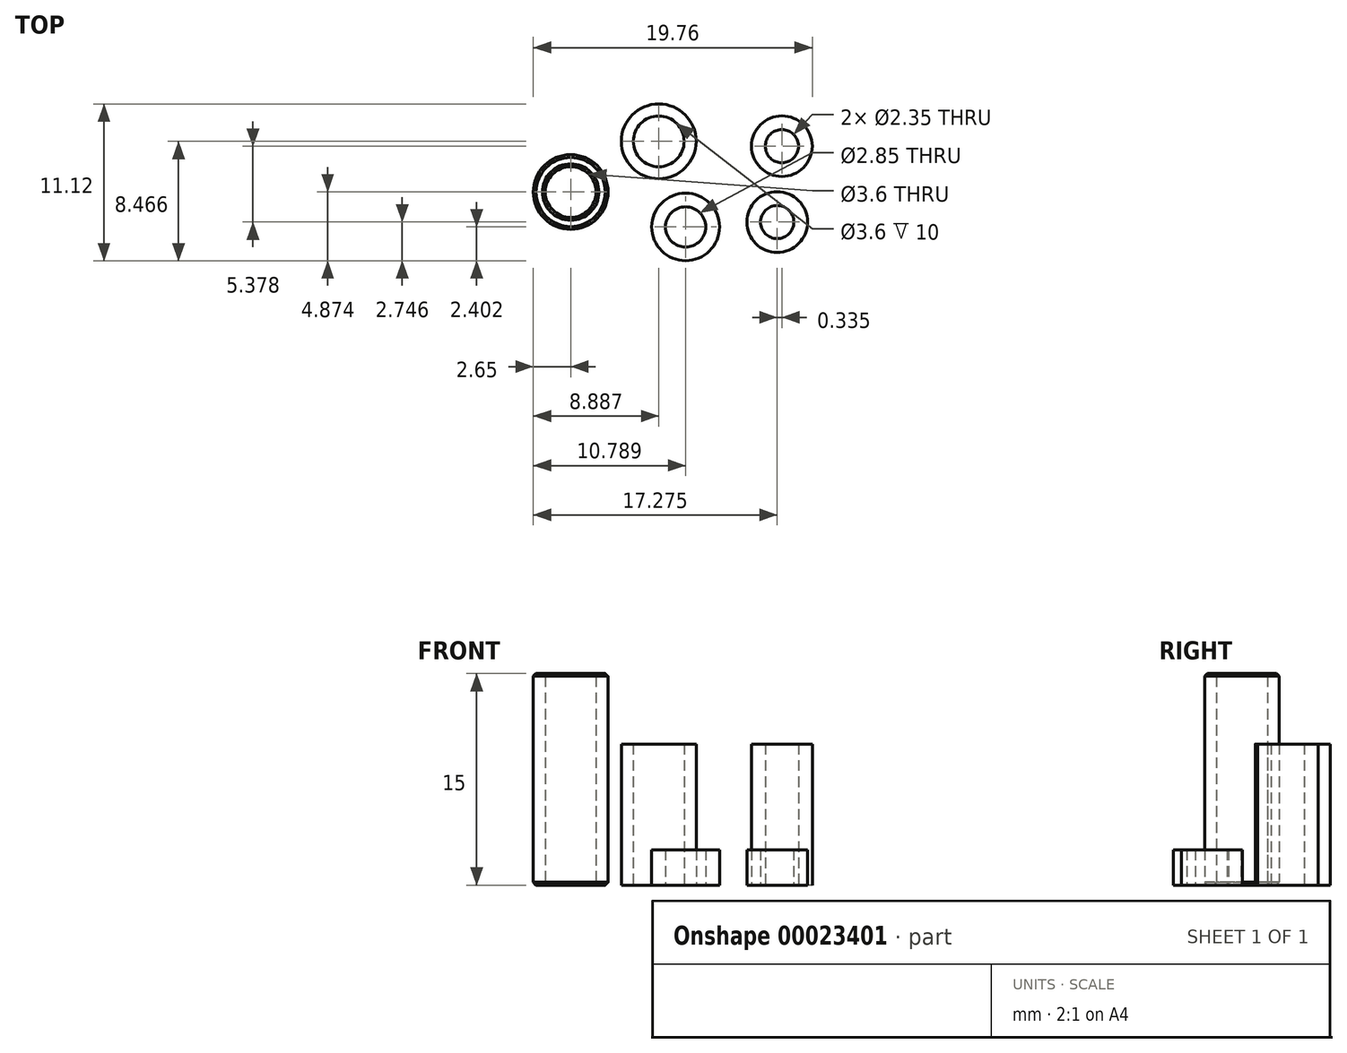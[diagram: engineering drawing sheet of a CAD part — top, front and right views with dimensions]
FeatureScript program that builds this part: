
annotation { "Feature Type Name" : "Feature", "Feature Type Description" : "" }
export const myFeature = defineFeature(function(context is Context, id is Id, definition is map)
    precondition{}
    {
        {
            var Q0;
            Q0=qCreatedBy(makeId("Top.planeOp"),FACE);
            var sketch = newSketch(context, id + "F0", { "sketchPlane" : qUnion([Q0])});
            skCircle(sketch, "E0", {"center": v(-1.3, 3.14) * mm, "radius": 1.8 * mm});
            skCircle(sketch, "E1", {"center": v(7.42, 2.8) * mm, "radius": 1.18 * mm});
            skCircle(sketch, "E2", {"center": v(-1.3, 3.14) * mm, "radius": 2.65 * mm});
            skCircle(sketch, "E3", {"center": v(7.42, 2.8) * mm, "radius": 2.15 * mm});
            skCircle(sketch, "E4", {"center": v(7.09, -2.58) * mm, "radius": 1.18 * mm});
            skCircle(sketch, "E5", {"center": v(7.09, -2.58) * mm, "radius": 2.15 * mm});
            skCircle(sketch, "E6", {"center": v(0.6, -2.93) * mm, "radius": 2.4 * mm});
            skCircle(sketch, "E7", {"center": v(0.6, -2.93) * mm, "radius": 1.43 * mm});
            skCircle(sketch, "E8", {"center": v(-7.54, -0.46) * mm, "radius": 1.8 * mm});
            skCircle(sketch, "E9", {"center": v(-7.54, -0.46) * mm, "radius": 2.65 * mm});
            skSolve(sketch);
        }
        {
            var Q0;
            Q0=makeQuery(id+"F0.imprint","IMPRINT",FACE,{"disambiguationData":[TD([[makeQuery(id+"F0.imprint","IMPRINT",EDGE,{"derivedFrom":sQuery(id+"F0.wireOp",EDGE,"E0")}),-1.0]])]});
            var Q1;
            Q1=makeQuery(id+"F0.imprint","IMPRINT",FACE,{"disambiguationData":[TD([[makeQuery(id+"F0.imprint","IMPRINT",EDGE,{"derivedFrom":sQuery(id+"F0.wireOp",EDGE,"E1")}),-1.0]])]});
            extrude(context, id + "F1", {"entities" : qUnion([Q0, Q1]), "depth" : 10 * mm});
        }
        {
            var Q0;
            Q0=makeQuery(id+"F0.imprint","IMPRINT",FACE,{"disambiguationData":[TD([[makeQuery(id+"F0.imprint","IMPRINT",EDGE,{"derivedFrom":sQuery(id+"F0.wireOp",EDGE,"E4")}),-1.0]])]});
            var Q1;
            Q1=makeQuery(id+"F0.imprint","IMPRINT",FACE,{"disambiguationData":[TD([[makeQuery(id+"F0.imprint","IMPRINT",EDGE,{"derivedFrom":sQuery(id+"F0.wireOp",EDGE,"E6")}),1.0]])]});
            extrude(context, id + "F2", {"entities" : qUnion([Q0, Q1]), "depth" : 2.5 * mm});
        }
        {
            var Q0;
            Q0=makeQuery(id+"F0.imprint","IMPRINT",FACE,{"disambiguationData":[TD([[makeQuery(id+"F0.imprint","IMPRINT",EDGE,{"derivedFrom":sQuery(id+"F0.wireOp",EDGE,"E8")}),-1.0]])]});
            extrude(context, id + "F3", {"entities" : qUnion([Q0]), "depth" : 15 * mm});
        }
        {
            var Q0;
            Q0=makeQuery(id+"F3.opExtrude","CAP_EDGE",EDGE,{"disambiguationData":[OSD([sQuery(id+"F0.wireOp",EDGE,"E8")])],"isStart":false});
            var Q1;
            Q1=makeQuery(id+"F3.opExtrude","CAP_EDGE",EDGE,{"disambiguationData":[OSD([sQuery(id+"F0.wireOp",EDGE,"E9")])],"isStart":false});
            var Q2;
            Q2=makeQuery(id+"F3.opExtrude","CAP_EDGE",EDGE,{"disambiguationData":[OSD([sQuery(id+"F0.wireOp",EDGE,"E8")])],"isStart":true});
            var Q3;
            Q3=makeQuery(id+"F3.opExtrude","CAP_EDGE",EDGE,{"disambiguationData":[OSD([sQuery(id+"F0.wireOp",EDGE,"E9")])],"isStart":true});
            chamfer(context, id + "F4", {"entities" : qUnion([Q0, Q1, Q2, Q3]), "width" : .2 * mm, "tangentPropagation" : true});
        }
    });
